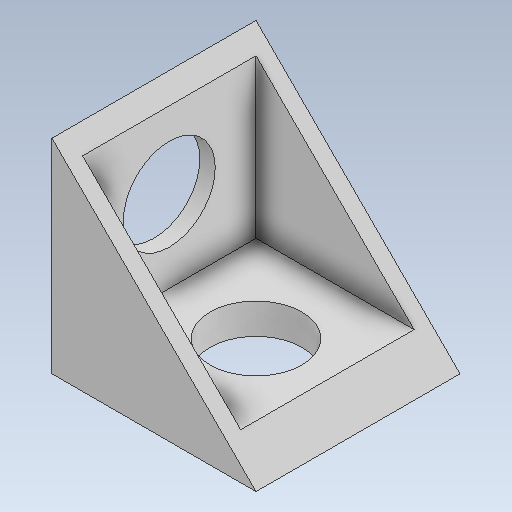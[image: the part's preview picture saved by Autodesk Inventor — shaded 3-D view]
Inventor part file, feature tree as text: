
AUTODESK INVENTOR PART (.ipt)
format: ipt  version: 2023 (Build 270158000, 158)  size: 126,464 bytes
history: native  units: in
note: dims shown in document units (in); Inventor stores cm internally (conversion verified against a paired STEP export)
features: sketch x5, other x3
ambient origin geometry x8: Origin, YZ Plane, XZ Plane, XY Plane, X Axis, Y Axis, Z Axis, Center Point
bodies: Solid1 (feature_tree)
feature tree (8):
  other  "CH-1-01-Cornerbracket.ipt"
  other  "Solid1::CH-1-01-Cornerbracket.ipt"
  other  "TaggingFeature1"
  sketch  "Sketch1"  dims[d0=0.3937in]
  sketch  "Sketch2"
  sketch  "Sketch6"
  sketch  "Sketch7"
  sketch  "Sketch8"
